# Revit family: QF_ELECTROLUXPROFESSIONAL_588026_MAIHABEOAO
name_source: partatom
category: Specialty Equipment
units: mm (PartAtom-declared; Revit-internal decimal feet)

## family parameters
Always vertical = Yes
Cut with Voids When Loaded = Yes
Enable Cutting in Views = No
Maintain Annotation Orientation = No
Part Type = Normal
Room Calculation Point = No
Round Connector Dimension = Use Diameter
Shared = No
Work Plane-Based = No

## types (1)
- QF_ELECTROLUXPROFESSIONAL_588026_MAIHABEOAO
    Conn Conduit = Yes
    Default Elevation = 0 mm  [stored 0 ft]
    Description = INDUCTION WOK,1 ZONE,1S,BS,500X800X250H
    Direct Waste Size = 0"
    Electrical Remarks = 400 V/3N ph/50/60 Hz
    HP = 6.7 HP
    Max Overcurrent Protection = 0 A
    Min Ckt Ampacity = 0 A
    Model = 588026
    Phase = 3
    Volts = 400 V
    Watts = 5000 W

note: [stored X ft] marks values corroborated as IEEE doubles in the binary element streams (Revit-internal decimal feet)

## geometry (parser evidence)
native form markers: Blend x16, Sweep x7
no freeform markers — native parametric forms only
